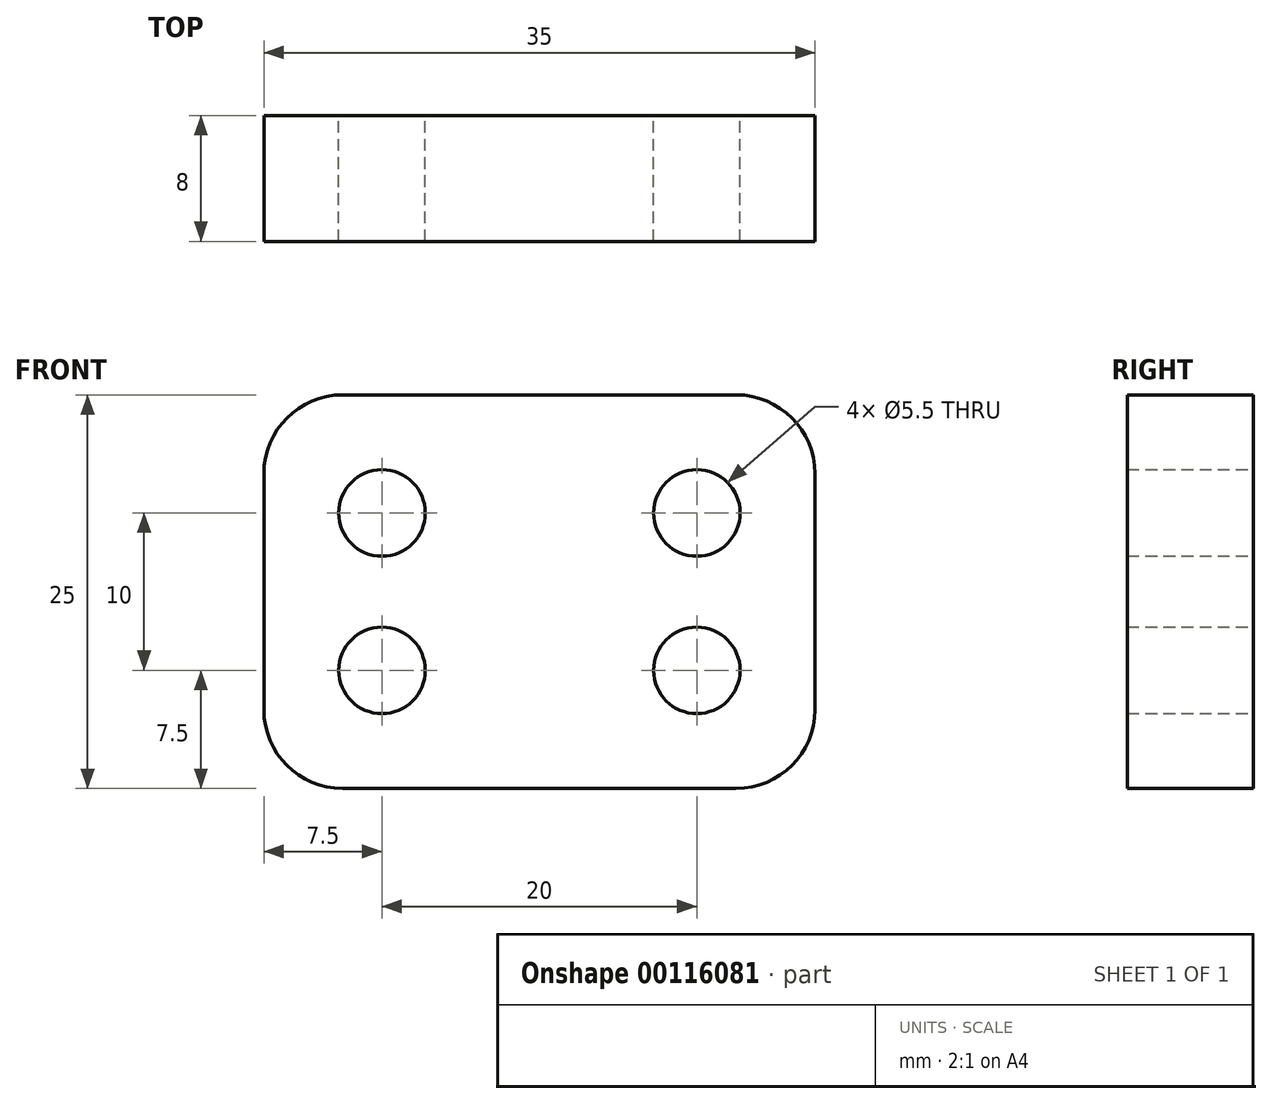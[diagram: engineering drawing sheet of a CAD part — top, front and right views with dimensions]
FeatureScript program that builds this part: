
annotation { "Feature Type Name" : "Feature", "Feature Type Description" : "" }
export const myFeature = defineFeature(function(context is Context, id is Id, definition is map)
    precondition{}
    {
        {
            var Q0;
            Q0=qCreatedBy(makeId("Front.planeOp"),FACE);
            var sketch = newSketch(context, id + "F0", { "sketchPlane" : qUnion([Q0])});
            skLineSegment(sketch, "E0.bottom", {"start": v(17.5, 12.5) * mm, "end": v(-17.5, 12.5) * mm});
            skLineSegment(sketch, "E0.top", {"start": v(17.5, -12.5) * mm, "end": v(-17.5, -12.5) * mm});
            skLineSegment(sketch, "E0.left", {"start": v(17.5, 12.5) * mm, "end": v(17.5, -12.5) * mm});
            skLineSegment(sketch, "E0.right", {"start": v(-17.5, 12.5) * mm, "end": v(-17.5, -12.5) * mm});
            skPoint(sketch, "E0.middle", {"position": v(0, 0) * mm});
            skCircle(sketch, "E1", {"center": v(-10, 5) * mm, "radius": 2.75 * mm});
            skCircle(sketch, "E2", {"center": v(-10, -5) * mm, "radius": 2.75 * mm});
            skLineSegment(sketch, "E3", {"start": v(0, 0) * mm, "end": v(0, 12.02) * mm, "construction": true});
            skLineSegment(sketch, "E4", {"start": v(0, 0) * mm, "end": v(25.4, 0) * mm, "construction": true});
            skCircle(sketch, "E5.MirrorC", {"center": v(10, -5) * mm, "radius": 2.75 * mm});
            skCircle(sketch, "E6.MirrorC", {"center": v(10, 5) * mm, "radius": 2.75 * mm});
            skSolve(sketch);
        }
        {
            var Q0;
            Q0=makeQuery(id+"F0.imprint","IMPRINT",FACE,{"disambiguationData":[TD([[makeQuery(id+"F0.imprint","IMPRINT",EDGE,{"derivedFrom":sQuery(id+"F0.wireOp",EDGE,"E0.bottom")}),1.0]])]});
            extrude(context, id + "F1", {"entities" : qUnion([Q0]), "depth" : 8 * mm});
        }
        {
            var Q0;
            Q0=makeQuery(id+"F1.opExtrude","SWEPT_EDGE",EDGE,{"disambiguationData":[OSD([sQuery(id+"F0.wireOp",EDGE,"E0.top"),sQuery(id+"F0.wireOp",EDGE,"E0.left")])]});
            var Q1;
            Q1=makeQuery(id+"F1.opExtrude","SWEPT_EDGE",EDGE,{"disambiguationData":[OSD([sQuery(id+"F0.wireOp",EDGE,"E0.bottom"),sQuery(id+"F0.wireOp",EDGE,"E0.left")])]});
            var Q2;
            Q2=makeQuery(id+"F1.opExtrude","SWEPT_EDGE",EDGE,{"disambiguationData":[OSD([sQuery(id+"F0.wireOp",EDGE,"E0.top"),sQuery(id+"F0.wireOp",EDGE,"E0.right")])]});
            var Q3;
            Q3=makeQuery(id+"F1.opExtrude","SWEPT_EDGE",EDGE,{"disambiguationData":[OSD([sQuery(id+"F0.wireOp",EDGE,"E0.bottom"),sQuery(id+"F0.wireOp",EDGE,"E0.right")])]});
            fillet(context, id + "F2", {"entities" : qUnion([Q0, Q1, Q2, Q3]), "radius" : 5 * mm, "tangentPropagation" : true, "allowEdgeOverflow" : false});
        }
    });
